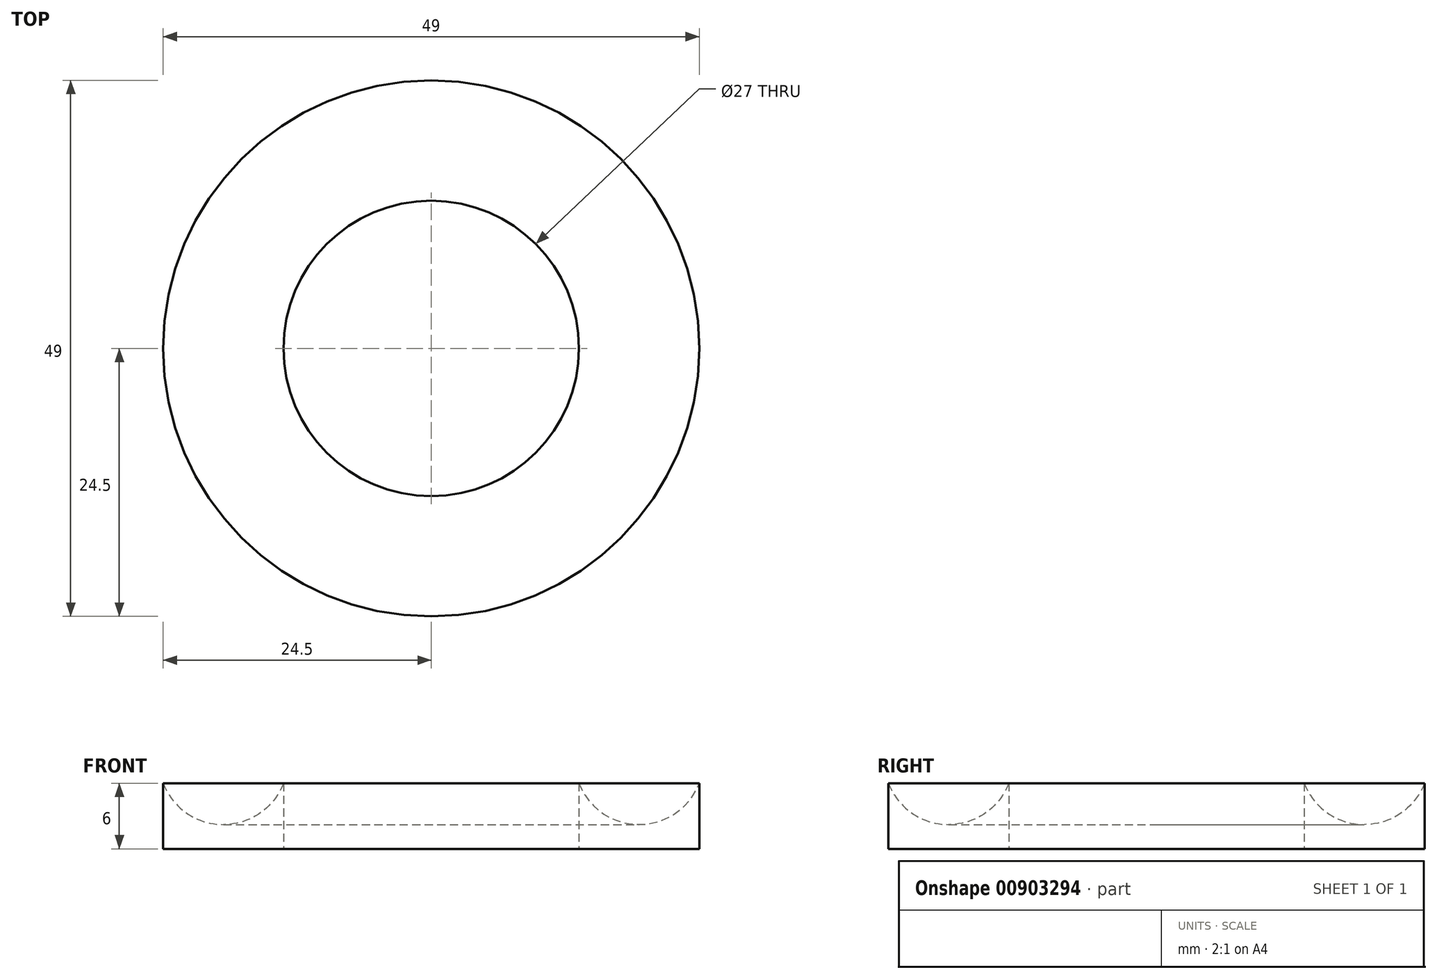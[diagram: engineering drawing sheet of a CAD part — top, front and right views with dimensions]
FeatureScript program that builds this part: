
annotation { "Feature Type Name" : "Feature", "Feature Type Description" : "" }
export const myFeature = defineFeature(function(context is Context, id is Id, definition is map)
    precondition{}
    {
        {
            var Q0;
            Q0=qCreatedBy(makeId("Top.planeOp"),FACE);
            var sketch = newSketch(context, id + "F0", { "sketchPlane" : qUnion([Q0])});
            skCircle(sketch, "E0", {"center": v(0, 0) * mm, "radius": 13.5 * mm});
            skCircle(sketch, "E1", {"center": v(0, 0) * mm, "radius": 24.5 * mm});
            skSolve(sketch);
        }
        {
            var Q0;
            Q0=makeQuery(id+"F0.imprint","IMPRINT",FACE,{"disambiguationData":[TD([[makeQuery(id+"F0.imprint","IMPRINT",EDGE,{"derivedFrom":sQuery(id+"F0.wireOp",EDGE,"E0")}),-1.0]])]});
            extrude(context, id + "F1", {"entities" : qUnion([Q0]), "depth" : 2 * mm, "offsetDistance" : 25 * mm});
        }
        {
            var Q0;
            Q0=qCreatedBy(makeId("Front.planeOp"),FACE);
            var sketch = newSketch(context, id + "F2", { "sketchPlane" : qUnion([Q0])});
            skLineSegment(sketch, "E2", {"start": v(0, 0) * mm, "end": v(13.5, 0) * mm, "construction": true});
            skLineSegment(sketch, "E3", {"start": v(24.5, 0) * mm, "end": v(13.5, 0) * mm});
            skLineSegment(sketch, "E4", {"start": v(13.5, 0) * mm, "end": v(13.5, 6) * mm});
            skLineSegment(sketch, "E5", {"start": v(24.5, 0) * mm, "end": v(24.5, 6) * mm});
            skArc(sketch, "E6", {"start": v(13.5, 6) * mm, "mid": v(19, 2.22) * mm, "end": v(24.5, 6) * mm});
            skLineSegment(sketch, "E7", {"start": v(0, 55.63) * mm, "end": v(0, -55.25) * mm, "construction": true});
            skSolve(sketch);
        }
        {
            var Q0;
            Q0=makeQuery(id+"F2.imprint","IMPRINT",FACE,{"disambiguationData":[TD([[makeQuery(id+"F2.imprint","IMPRINT",EDGE,{"derivedFrom":sQuery(id+"F2.wireOp",EDGE,"E3")}),-1.0]])]});
            var Q1;
            Q1=sQuery(id+"F2.wireOp",EDGE,"E7");
            revolve(context, id + "F3", {"operationType" : NewBodyOperationType.ADD, "surfaceOperationType" : NewSurfaceOperationType.NEW, "entities" : qUnion([Q0]), "axis" : qUnion([Q1]), "revolveType" : RevolveType.FULL});
        }
    });
